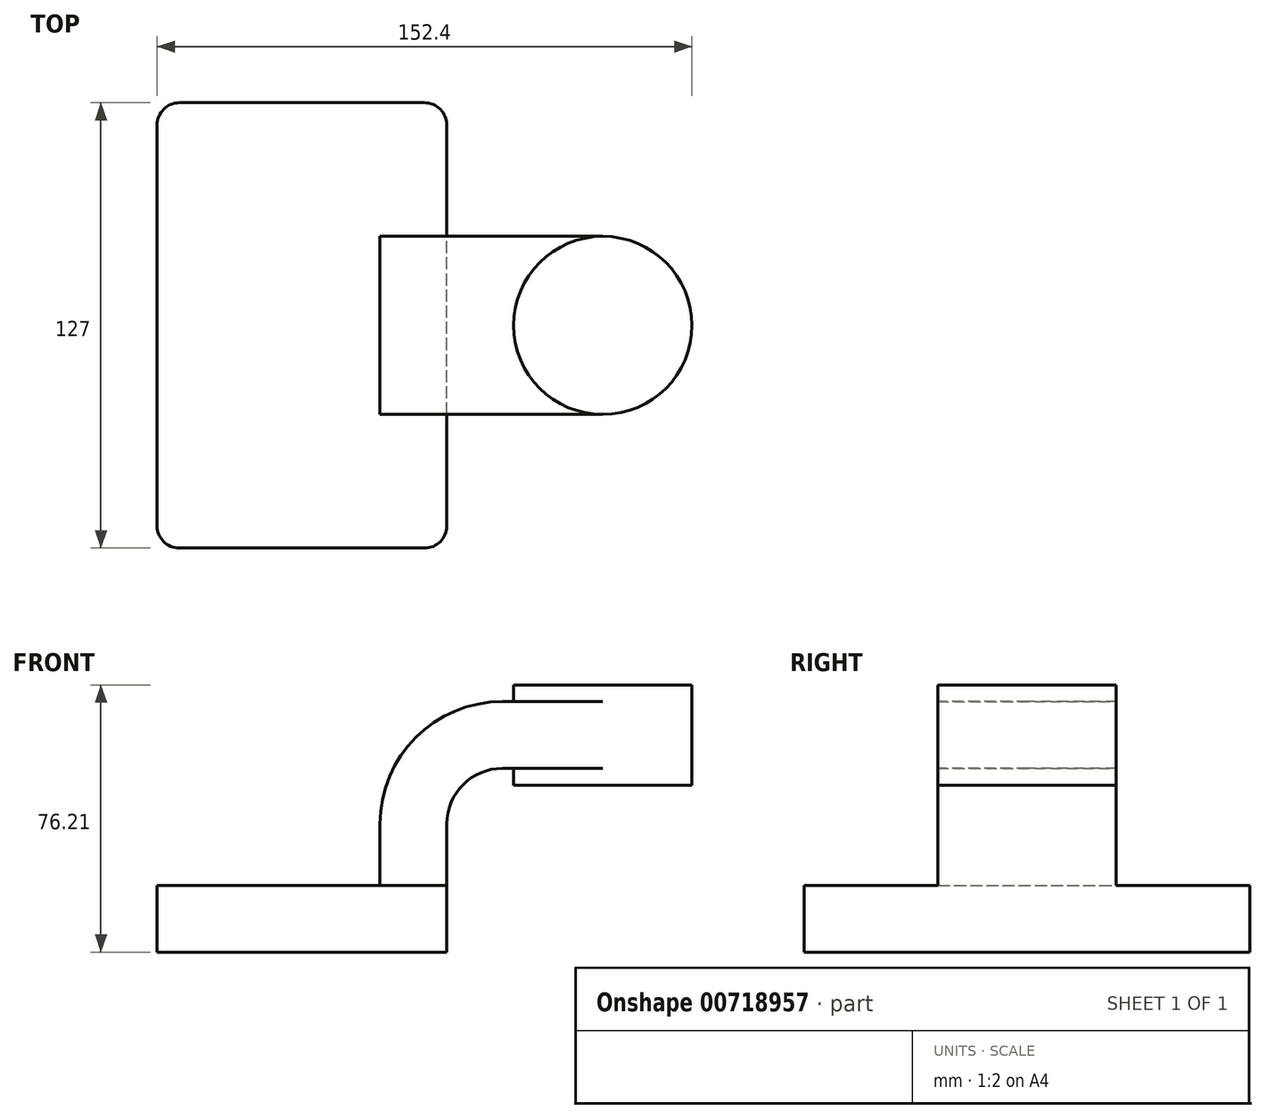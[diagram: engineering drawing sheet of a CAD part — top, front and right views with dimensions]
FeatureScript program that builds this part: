
annotation { "Feature Type Name" : "Feature", "Feature Type Description" : "" }
export const myFeature = defineFeature(function(context is Context, id is Id, definition is map)
    precondition{}
    {
        {
            var Q0;
            Q0=qCreatedBy(makeId("Front.planeOp"),FACE);
            var sketch = newSketch(context, id + "F0", { "sketchPlane" : qUnion([Q0])});
            skLineSegment(sketch, "E0.bottom", {"start": v(-41.28, 9.53) * mm, "end": v(41.28, 9.53) * mm});
            skLineSegment(sketch, "E0.top", {"start": v(-41.28, -9.53) * mm, "end": v(41.28, -9.53) * mm});
            skLineSegment(sketch, "E0.left", {"start": v(-41.28, 9.53) * mm, "end": v(-41.28, -9.53) * mm});
            skLineSegment(sketch, "E0.right", {"start": v(41.28, 9.53) * mm, "end": v(41.28, -9.53) * mm});
            skPoint(sketch, "E0.middle", {"position": v(0, 0) * mm});
            skLineSegment(sketch, "E1.bottom", {"start": v(60.33, 66.67) * mm, "end": v(111.12, 66.67) * mm});
            skLineSegment(sketch, "E1.top", {"start": v(60.33, 38.1) * mm, "end": v(111.12, 38.1) * mm});
            skLineSegment(sketch, "E1.left", {"start": v(60.33, 66.68) * mm, "end": v(60.33, 38.1) * mm});
            skLineSegment(sketch, "E1.right", {"start": v(111.12, 66.68) * mm, "end": v(111.12, 38.1) * mm});
            skPoint(sketch, "E1.middle", {"position": v(85.72, 52.39) * mm});
            skLineSegment(sketch, "E2", {"start": v(41.28, 9.53) * mm, "end": v(41.28, 27) * mm});
            skArc(sketch, "E3", {"start": v(41.28, 27) * mm, "mid": v(45.92, 38.23) * mm, "end": v(57.15, 42.88) * mm});
            skLineSegment(sketch, "E4", {"start": v(57.15, 42.88) * mm, "end": v(85.72, 42.88) * mm});
            skLineSegment(sketch, "E5.0", {"start": v(57.15, 61.93) * mm, "end": v(85.72, 61.93) * mm});
            skArc(sketch, "E5.1", {"start": v(22.22, 27) * mm, "mid": v(32.45, 51.7) * mm, "end": v(57.15, 61.93) * mm});
            skLineSegment(sketch, "E5.2", {"start": v(22.22, 9.53) * mm, "end": v(22.22, 27) * mm});
            skLineSegment(sketch, "E6", {"start": v(85.72, 38.1) * mm, "end": v(85.72, 66.67) * mm});
            skFitSpline(sketch, "E7", {"points": [v(-41.28, 9.53) * mm, v(57.15, 61.93) * mm], "startDerivative": vector(0, 100.05) * mm, "endDerivative": vector(104.78, 0) * mm});
            skSolve(sketch);
        }
        {
            var Q0;
            Q0=makeQuery(id+"F0.imprint","IMPRINT",FACE,{"disambiguationData":[TD([[makeQuery(id+"F0.imprint","IMPRINT",EDGE,{"derivedFrom":sQuery(id+"F0.wireOp",EDGE,"E0.top")}),1.0]])]});
            extrude(context, id + "F1", {"entities" : qUnion([Q0]), "endBound" : BoundingType.SYMMETRIC, "depth" : 127 * mm, "offsetDistance" : 25.4 * mm});
        }
        {
            var Q0;
            {var subQ1=sQuery(id+"F0.wireOp",EDGE,"E2");Q0=makeQuery(id+"F0.imprint","IMPRINT",FACE,{"disambiguationData":[TD([[makeQuery(id+"F0.imprint","IMPRINT",EDGE,{"derivedFrom":subQ1}),1.0]])]});}
            var Q1;
            {var subQ0=sQuery(id+"F0.wireOp",EDGE,"E5.0");var subQ1=sQuery(id+"F0.wireOp",EDGE,"E1.left");var subQ2=makeQuery(id+"F0.imprint","INTERSECT",VERTEX,{"derivedFrom":[subQ1,subQ0]});Q1=makeQuery(id+"F0.imprint","IMPRINT",FACE,{"disambiguationData":[TD([[makeQuery(id+"F0.imprint","IMPRINT",EDGE,{"disambiguationData":[TD([[subQ2,-1.0]])],"derivedFrom":subQ1}),1.0]])]});}
            extrude(context, id + "F2", {"entities" : qUnion([Q0, Q1]), "operationType" : NewBodyOperationType.ADD, "endBound" : BoundingType.SYMMETRIC, "depth" : 50.8 * mm, "offsetDistance" : 25.4 * mm});
        }
        {
            var Q0;
            Q0=makeQuery(id+"F0.imprint","IMPRINT",FACE,{"disambiguationData":[TD([[makeQuery(id+"F0.imprint","IMPRINT",EDGE,{"derivedFrom":sQuery(id+"F0.wireOp",EDGE,"E5.1")}),1.0]])]});
            extrude(context, id + "F3", {"entities" : qUnion([Q0]), "operationType" : NewBodyOperationType.ADD, "endBound" : BoundingType.SYMMETRIC, "depth" : 15.88 * mm, "offsetDistance" : 25.4 * mm});
        }
        {
            var Q0;
            {var subQ0=sQuery(id+"F0.wireOp",EDGE,"E1.right");Q0=makeQuery(id+"F0.imprint","IMPRINT",FACE,{"disambiguationData":[TD([[makeQuery(id+"F0.imprint","IMPRINT",EDGE,{"derivedFrom":subQ0}),-1.0]])]});}
            var Q1;
            Q1=sQuery(id+"F0.wireOp",EDGE,"E6");
            revolve(context, id + "F4", {"operationType" : NewBodyOperationType.ADD, "surfaceOperationType" : NewSurfaceOperationType.NEW, "entities" : qUnion([Q0]), "axis" : qUnion([Q1]), "revolveType" : RevolveType.FULL});
        }
        {
            var Q0;
            Q0=makeQuery(id+"F1.opExtrude","CAP_EDGE",EDGE,{"disambiguationData":[OSD([sQuery(id+"F0.wireOp",EDGE,"E0.right")])],"isStart":false});
            var Q1;
            Q1=makeQuery(id+"F1.opExtrude","CAP_EDGE",EDGE,{"disambiguationData":[OSD([sQuery(id+"F0.wireOp",EDGE,"E0.left")])],"isStart":false});
            var Q2;
            Q2=makeQuery(id+"F1.opExtrude","CAP_EDGE",EDGE,{"disambiguationData":[OSD([sQuery(id+"F0.wireOp",EDGE,"E0.right")])],"isStart":true});
            var Q3;
            Q3=makeQuery(id+"F1.opExtrude","CAP_EDGE",EDGE,{"disambiguationData":[OSD([sQuery(id+"F0.wireOp",EDGE,"E0.left")])],"isStart":true});
            fillet(context, id + "F5", {"entities" : qUnion([Q0, Q1, Q2, Q3]), "radius" : 6.35 * mm, "tangentPropagation" : true, "allowEdgeOverflow" : false});
        }
    });
